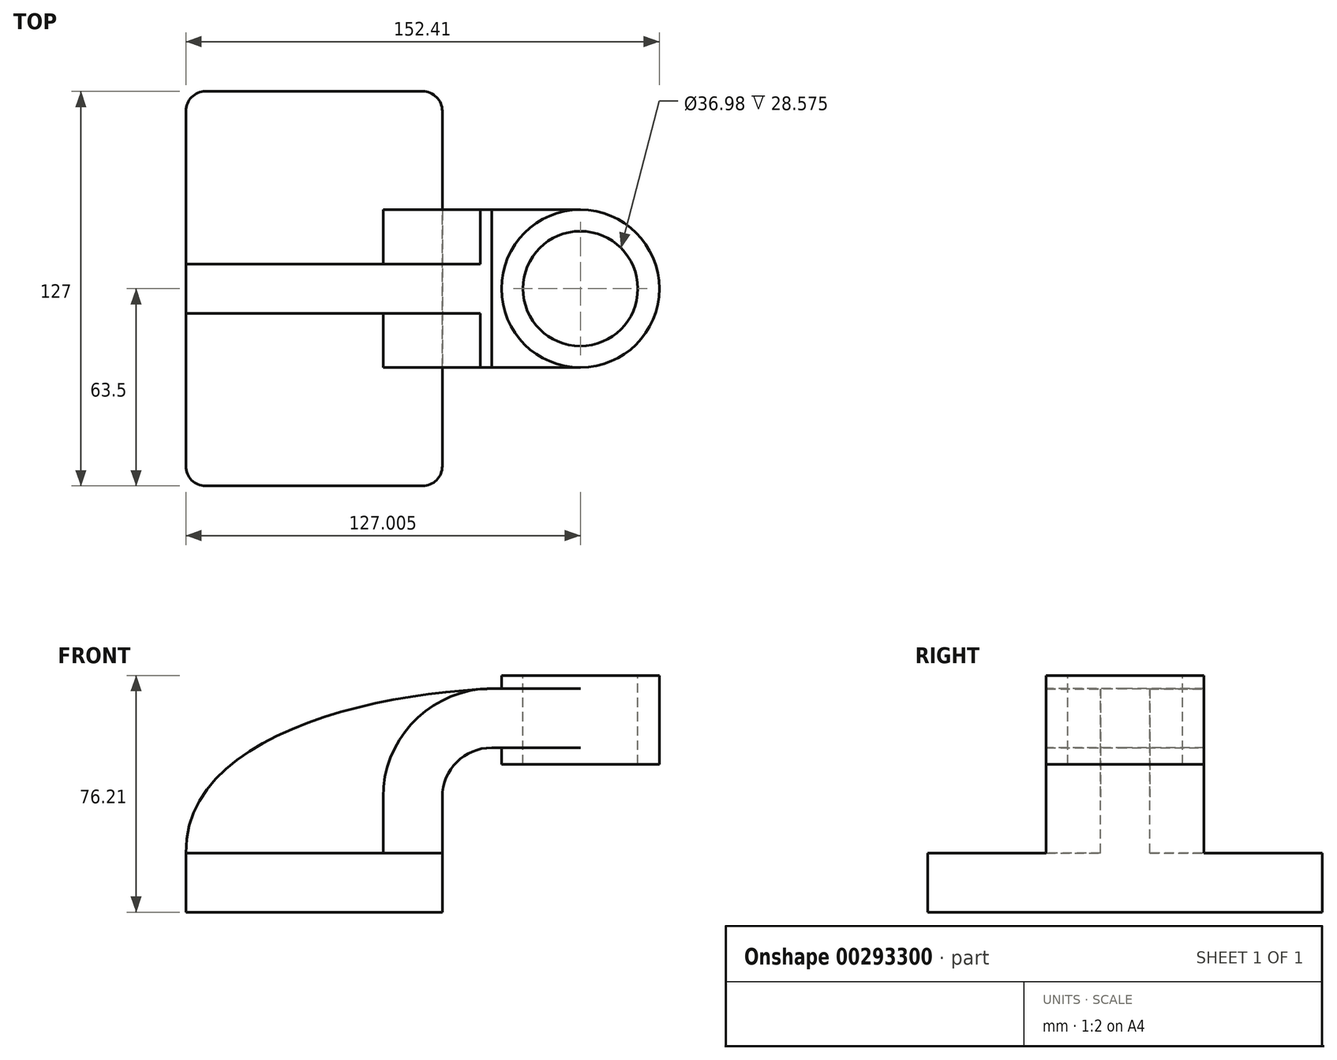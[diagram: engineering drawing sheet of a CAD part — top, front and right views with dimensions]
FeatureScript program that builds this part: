
annotation { "Feature Type Name" : "Feature", "Feature Type Description" : "" }
export const myFeature = defineFeature(function(context is Context, id is Id, definition is map)
    precondition{}
    {
        {
            var Q0;
            Q0=qCreatedBy(makeId("Front.planeOp"),FACE);
            var sketch = newSketch(context, id + "F0", { "sketchPlane" : qUnion([Q0])});
            skLineSegment(sketch, "E0.bottom", {"start": v(41.28, 9.53) * mm, "end": v(-41.28, 9.53) * mm});
            skLineSegment(sketch, "E0.top", {"start": v(41.28, -9.52) * mm, "end": v(-41.28, -9.52) * mm});
            skLineSegment(sketch, "E0.left", {"start": v(41.28, 9.53) * mm, "end": v(41.28, -9.52) * mm});
            skLineSegment(sketch, "E0.right", {"start": v(-41.28, 9.53) * mm, "end": v(-41.28, -9.52) * mm});
            skPoint(sketch, "E0.middle", {"position": v(0, 0) * mm});
            skLineSegment(sketch, "E1.bottom", {"start": v(111.12, 66.68) * mm, "end": v(60.32, 66.68) * mm});
            skLineSegment(sketch, "E1.top", {"start": v(111.12, 38.1) * mm, "end": v(60.32, 38.1) * mm});
            skLineSegment(sketch, "E1.left", {"start": v(111.12, 66.68) * mm, "end": v(111.12, 38.1) * mm});
            skLineSegment(sketch, "E1.right", {"start": v(60.32, 66.68) * mm, "end": v(60.32, 38.1) * mm});
            skPoint(sketch, "E1.middle", {"position": v(85.72, 52.39) * mm});
            skLineSegment(sketch, "E2", {"start": v(41.28, 9.53) * mm, "end": v(41.28, 27.5) * mm});
            skArc(sketch, "E3", {"start": v(41.27, 27.5) * mm, "mid": v(45.92, 38.73) * mm, "end": v(57.15, 43.38) * mm});
            skLineSegment(sketch, "E4", {"start": v(57.15, 43.38) * mm, "end": v(85.72, 43.38) * mm});
            skPoint(sketch, "E4.endSnap0", {"position": v(85.72, 38.1) * mm});
            skLineSegment(sketch, "E5.0", {"start": v(57.15, 62.43) * mm, "end": v(85.72, 62.43) * mm});
            skArc(sketch, "E5.1", {"start": v(22.23, 27.5) * mm, "mid": v(32.45, 52.2) * mm, "end": v(57.15, 62.43) * mm});
            skLineSegment(sketch, "E5.2", {"start": v(22.23, 9.53) * mm, "end": v(22.23, 27.5) * mm});
            skLineSegment(sketch, "E6", {"start": v(85.72, 38.1) * mm, "end": v(85.72, 66.68) * mm});
            skFitSpline(sketch, "E7", {"points": [v(-41.28, 9.52) * mm, v(57.15, 62.43) * mm], "startDerivative": vector(-0.87, 110.2) * mm, "endDerivative": vector(126.08, 5.54) * mm});
            skSolve(sketch);
        }
        {
            var Q0;
            Q0=makeQuery(id+"F0.imprint","IMPRINT",FACE,{"disambiguationData":[TD([[makeQuery(id+"F0.imprint","IMPRINT",EDGE,{"derivedFrom":sQuery(id+"F0.wireOp",EDGE,"E0.top")}),-1.0]])]});
            extrude(context, id + "F1", {"entities" : qUnion([Q0]), "flatOperationType" : FlatOperationType.REMOVE, "oppositeDirection" : true, "offsetDistance" : 25 * mm, "depth" : 127 * mm, "domain" : OperationDomain.MODEL, "symmetric" : true});
        }
        {
            var Q0;
            {var subQ1=sQuery(id+"F0.wireOp",EDGE,"E2");Q0=makeQuery(id+"F0.imprint","IMPRINT",FACE,{"disambiguationData":[TD([[makeQuery(id+"F0.imprint","IMPRINT",EDGE,{"derivedFrom":subQ1}),1.0]])]});}
            var Q1;
            {var subQ0=sQuery(id+"F0.wireOp",EDGE,"E5.0");var subQ1=sQuery(id+"F0.wireOp",EDGE,"E1.right");var subQ2=makeQuery(id+"F0.imprint","INTERSECT",VERTEX,{"derivedFrom":[subQ1,subQ0]});Q1=makeQuery(id+"F0.imprint","IMPRINT",FACE,{"disambiguationData":[TD([[makeQuery(id+"F0.imprint","IMPRINT",EDGE,{"disambiguationData":[TD([[subQ2,-1.0]])],"derivedFrom":subQ1}),1.0]])]});}
            extrude(context, id + "F2", {"entities" : qUnion([Q0, Q1]), "operationType" : NewBodyOperationType.ADD, "depth" : 50.8 * mm, "symmetric" : true});
        }
        {
            var Q0;
            {var subQ3=sQuery(id+"F0.wireOp",EDGE,"E5.2");Q0=makeQuery(id+"F0.imprint","IMPRINT",FACE,{"disambiguationData":[TD([[makeQuery(id+"F0.imprint","IMPRINT",EDGE,{"derivedFrom":subQ3}),1.0]])]});}
            extrude(context, id + "F3", {"entities" : qUnion([Q0]), "operationType" : NewBodyOperationType.ADD, "depth" : 15.88 * mm, "symmetric" : true});
        }
        {
            var Q0;
            {var subQ0=sQuery(id+"F0.wireOp",EDGE,"E1.left");Q0=makeQuery(id+"F0.imprint","IMPRINT",FACE,{"disambiguationData":[TD([[makeQuery(id+"F0.imprint","IMPRINT",EDGE,{"derivedFrom":subQ0}),-1.0]])]});}
            var Q1;
            Q1=sQuery(id+"F0.wireOp",EDGE,"E6");
            revolve(context, id + "F4", {"operationType" : NewBodyOperationType.ADD, "entities" : qUnion([Q0]), "axis" : qUnion([Q1]), "revolveType" : RevolveType.FULL});
        }
        {
            var Q0;
            Q0=makeQuery(id+"F1.opExtrude","CAP_EDGE",EDGE,{"disambiguationData":[OSD([sQuery(id+"F0.wireOp",EDGE,"E0.left")])],"isStart":true});
            var Q1;
            Q1=makeQuery(id+"F1.opExtrude","CAP_EDGE",EDGE,{"disambiguationData":[OSD([sQuery(id+"F0.wireOp",EDGE,"E0.right")])],"isStart":true});
            var Q2;
            Q2=makeQuery(id+"F1.opExtrude","CAP_EDGE",EDGE,{"disambiguationData":[OSD([sQuery(id+"F0.wireOp",EDGE,"E0.right")])],"isStart":false});
            var Q3;
            Q3=makeQuery(id+"F1.opExtrude","CAP_EDGE",EDGE,{"disambiguationData":[OSD([sQuery(id+"F0.wireOp",EDGE,"E0.left")])],"isStart":false});
            fillet(context, id + "F5", {"entities" : qUnion([Q0, Q1, Q2, Q3]), "radius" : 6.35 * mm, "tangentPropagation" : true, "allowEdgeOverflow" : false});
        }
        {
            var Q0;
            Q0=makeQuery(id+"F4.opRevolve","SWEPT_FACE",FACE,{"disambiguationData":[OSD([sQuery(id+"F0.wireOp",EDGE,"E1.bottom")])]});
            var sketch = newSketch(context, id + "F6", { "sketchPlane" : qUnion([Q0])});
            skCircle(sketch, "E8", {"center": v(85.72, 0) * mm, "radius": 18.49 * mm});
            skSolve(sketch);
        }
        {
            var Q0;
            Q0 = qSketchRegion(id + "F6", true);
            extrude(context, id + "F7", {"entities" : qUnion([Q0]), "operationType" : NewBodyOperationType.REMOVE, "oppositeDirection" : true, "depth" : 100.97 * mm});
        }
    });
